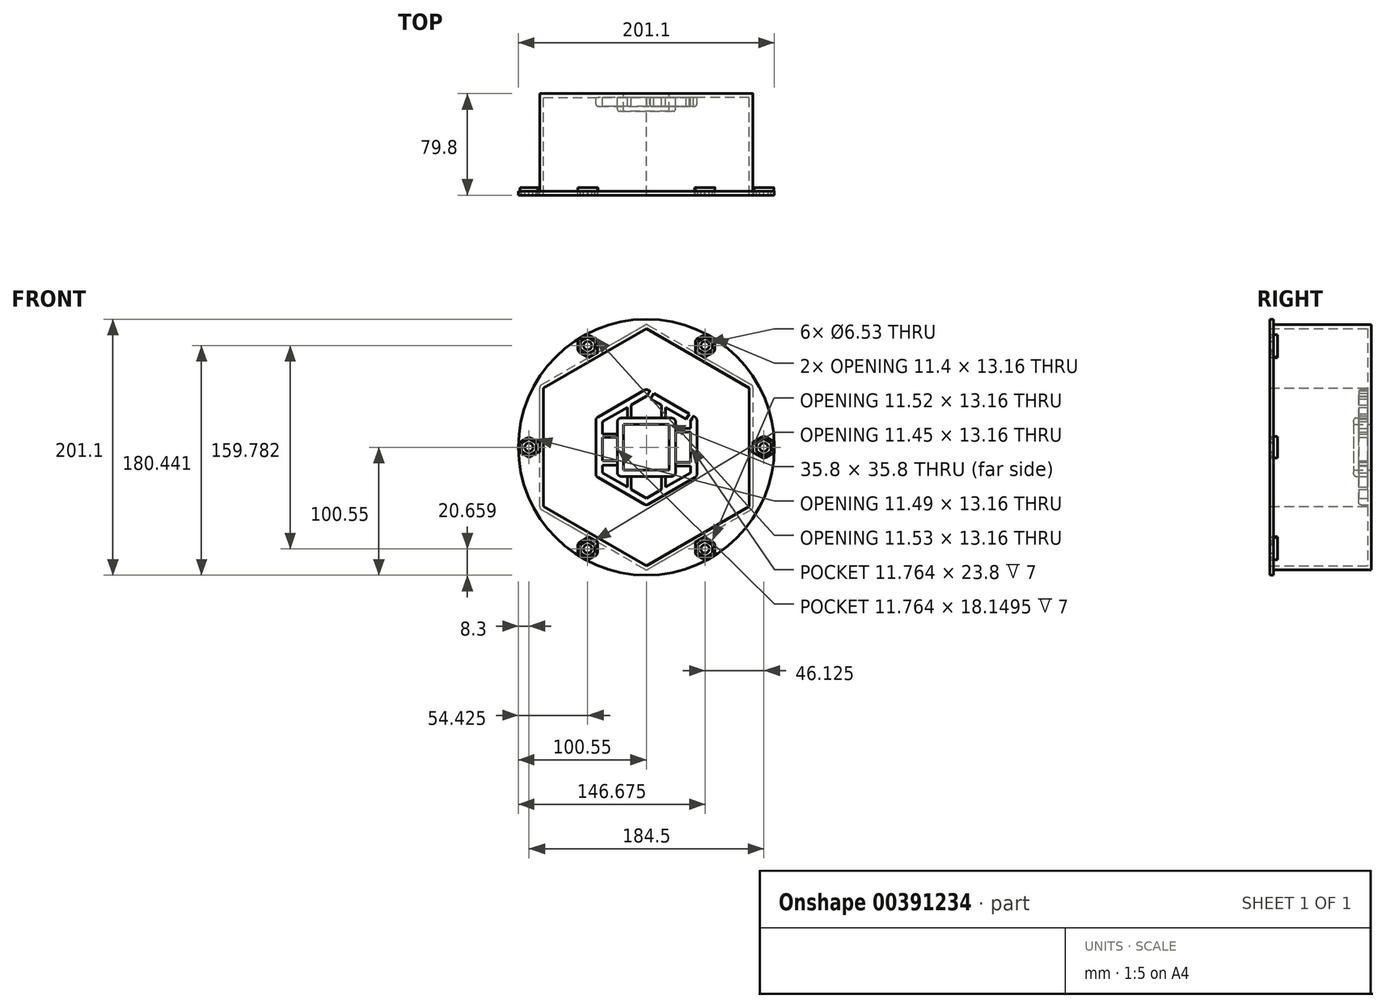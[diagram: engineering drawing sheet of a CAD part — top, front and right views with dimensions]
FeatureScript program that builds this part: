
annotation { "Feature Type Name" : "Feature", "Feature Type Description" : "" }
export const myFeature = defineFeature(function(context is Context, id is Id, definition is map)
    precondition{}
    {
        {
            var Q0;
            Q0=qCreatedBy(makeId("Front.planeOp"),FACE);
            var sketch = newSketch(context, id + "F0", { "sketchPlane" : qUnion([Q0])});
            skCircle(sketch, "E0.cCircle", {"center": v(0, 0) * mm, "radius": 80.75 * mm, "construction": true});
            skLineSegment(sketch, "E0.0", {"start": v(80.75, -46.62) * mm, "end": v(0, -93.24) * mm});
            skLineSegment(sketch, "E0.1", {"start": v(0, -93.24) * mm, "end": v(-80.75, -46.62) * mm});
            skLineSegment(sketch, "E0.2", {"start": v(-80.75, -46.62) * mm, "end": v(-80.75, 46.62) * mm});
            skLineSegment(sketch, "E0.3", {"start": v(-80.75, 46.62) * mm, "end": v(0, 93.24) * mm});
            skLineSegment(sketch, "E0.4", {"start": v(0, 93.24) * mm, "end": v(80.75, 46.62) * mm});
            skLineSegment(sketch, "E0.5", {"start": v(80.75, 46.62) * mm, "end": v(80.75, -46.62) * mm});
            skPoint(sketch, "E0.0.midPoint", {"position": v(40.38, -69.93) * mm});
            skCircle(sketch, "E1.cCircle", {"center": v(0, 0) * mm, "radius": 83.75 * mm, "construction": true});
            skLineSegment(sketch, "E1.0", {"start": v(83.75, 46.62) * mm, "end": v(83.75, -46.62) * mm});
            skLineSegment(sketch, "E1.1", {"start": v(82.25, -49.22) * mm, "end": v(1.5, -95.84) * mm});
            skLineSegment(sketch, "E1.2", {"start": v(-1.5, -95.84) * mm, "end": v(-82.25, -49.22) * mm});
            skLineSegment(sketch, "E1.3", {"start": v(-83.75, -46.62) * mm, "end": v(-83.75, 46.62) * mm});
            skLineSegment(sketch, "E1.4", {"start": v(-82.25, 49.22) * mm, "end": v(-1.5, 95.84) * mm});
            skLineSegment(sketch, "E1.5", {"start": v(1.5, 95.84) * mm, "end": v(82.25, 49.22) * mm});
            skPoint(sketch, "E1.0.midPoint", {"position": v(83.75, 0) * mm});
            skCircle(sketch, "E2", {"center": v(0, 0) * mm, "radius": 100.55 * mm});
            skCircle(sketch, "E3.cCircle", {"center": v(0, 0) * mm, "radius": 39.66 * mm, "construction": true});
            skLineSegment(sketch, "E3.0", {"start": v(38.16, -23.77) * mm, "end": v(1.5, -44.93) * mm});
            skLineSegment(sketch, "E3.1", {"start": v(-1.5, -44.93) * mm, "end": v(-38.16, -23.77) * mm});
            skLineSegment(sketch, "E3.2", {"start": v(-39.66, -21.17) * mm, "end": v(-39.66, 21.17) * mm});
            skLineSegment(sketch, "E3.3", {"start": v(-38.16, 23.77) * mm, "end": v(-1.5, 44.93) * mm});
            skLineSegment(sketch, "E3.4", {"start": v(1.5, 44.93) * mm, "end": v(38.16, 23.77) * mm});
            skLineSegment(sketch, "E3.5", {"start": v(39.66, 21.17) * mm, "end": v(39.66, -21.17) * mm});
            skPoint(sketch, "E3.0.midPoint", {"position": v(19.83, -34.35) * mm});
            skCircle(sketch, "E4.cCircle", {"center": v(0, 0) * mm, "radius": 34.66 * mm, "construction": true});
            skLineSegment(sketch, "E4.0", {"start": v(34.66, -20.01) * mm, "end": v(0, -40.03) * mm});
            skLineSegment(sketch, "E4.1", {"start": v(0, -40.03) * mm, "end": v(-34.66, -20.01) * mm});
            skLineSegment(sketch, "E4.2", {"start": v(-34.66, -20.01) * mm, "end": v(-34.66, 20.01) * mm});
            skLineSegment(sketch, "E4.3", {"start": v(-34.66, 20.01) * mm, "end": v(0, 40.03) * mm});
            skLineSegment(sketch, "E4.4", {"start": v(0, 40.03) * mm, "end": v(34.66, 20.01) * mm});
            skLineSegment(sketch, "E4.5", {"start": v(34.66, 20.01) * mm, "end": v(34.66, -20.01) * mm});
            skPoint(sketch, "E4.0.midPoint", {"position": v(17.33, -30.02) * mm});
            skPoint(sketch, "E5.visualSharp", {"position": v(0, 96.7) * mm});
            skArc(sketch, "E5.filletArc", {"start": v(1.5, 95.84) * mm, "mid": v(0, 96.24) * mm, "end": v(-1.5, 95.84) * mm});
            skPoint(sketch, "E6.visualSharp", {"position": v(83.75, 48.35) * mm});
            skArc(sketch, "E6.filletArc", {"start": v(83.75, 46.62) * mm, "mid": v(83.35, 48.12) * mm, "end": v(82.25, 49.22) * mm});
            skPoint(sketch, "E7.visualSharp", {"position": v(83.75, -48.35) * mm});
            skArc(sketch, "E7.filletArc", {"start": v(82.25, -49.22) * mm, "mid": v(83.35, -48.12) * mm, "end": v(83.75, -46.62) * mm});
            skPoint(sketch, "E8.visualSharp", {"position": v(0, -96.7) * mm});
            skArc(sketch, "E8.filletArc", {"start": v(-1.5, -95.84) * mm, "mid": v(0, -96.24) * mm, "end": v(1.5, -95.84) * mm});
            skPoint(sketch, "E9.visualSharp", {"position": v(-83.75, -48.35) * mm});
            skArc(sketch, "E9.filletArc", {"start": v(-83.75, -46.62) * mm, "mid": v(-83.35, -48.12) * mm, "end": v(-82.25, -49.22) * mm});
            skPoint(sketch, "E10.visualSharp", {"position": v(-83.75, 48.35) * mm});
            skArc(sketch, "E10.filletArc", {"start": v(-82.25, 49.22) * mm, "mid": v(-83.35, 48.12) * mm, "end": v(-83.75, 46.62) * mm});
            skPoint(sketch, "E11.visualSharp", {"position": v(39.66, 22.9) * mm});
            skArc(sketch, "E11.filletArc", {"start": v(39.66, 21.17) * mm, "mid": v(39.26, 22.67) * mm, "end": v(38.16, 23.77) * mm});
            skPoint(sketch, "E12.visualSharp", {"position": v(39.66, -22.9) * mm});
            skArc(sketch, "E12.filletArc", {"start": v(38.16, -23.77) * mm, "mid": v(39.26, -22.67) * mm, "end": v(39.66, -21.17) * mm});
            skPoint(sketch, "E13.visualSharp", {"position": v(0, -45.8) * mm});
            skArc(sketch, "E13.filletArc", {"start": v(-1.5, -44.93) * mm, "mid": v(0, -45.34) * mm, "end": v(1.5, -44.93) * mm});
            skPoint(sketch, "E14.visualSharp", {"position": v(-39.66, -22.9) * mm});
            skArc(sketch, "E14.filletArc", {"start": v(-39.66, -21.17) * mm, "mid": v(-39.26, -22.67) * mm, "end": v(-38.16, -23.77) * mm});
            skPoint(sketch, "E15.visualSharp", {"position": v(-39.66, 22.9) * mm});
            skArc(sketch, "E15.filletArc", {"start": v(-38.16, 23.77) * mm, "mid": v(-39.26, 22.67) * mm, "end": v(-39.66, 21.17) * mm});
            skPoint(sketch, "E16.visualSharp", {"position": v(0, 45.8) * mm});
            skArc(sketch, "E16.filletArc", {"start": v(1.5, 44.93) * mm, "mid": v(0, 45.34) * mm, "end": v(-1.5, 44.93) * mm});
            skPoint(sketch, "E17", {"position": v(-46.13, 79.9) * mm});
            skPoint(sketch, "E18", {"position": v(-92.25, 0) * mm});
            skPoint(sketch, "E19", {"position": v(-46.12, -79.9) * mm});
            skPoint(sketch, "E20", {"position": v(46.13, -79.9) * mm});
            skPoint(sketch, "E21", {"position": v(92.25, 0) * mm});
            skPoint(sketch, "E22", {"position": v(46.13, 79.9) * mm});
            skCircle(sketch, "E23.cCircle", {"center": v(92.25, 0) * mm, "radius": 5.7 * mm, "construction": true});
            skLineSegment(sketch, "E23.0", {"start": v(97.95, -3.3) * mm, "end": v(92.25, -6.58) * mm});
            skLineSegment(sketch, "E23.1", {"start": v(92.25, -6.58) * mm, "end": v(86.55, -3.3) * mm});
            skLineSegment(sketch, "E23.2", {"start": v(86.55, -3.3) * mm, "end": v(86.55, 3.3) * mm});
            skLineSegment(sketch, "E23.3", {"start": v(86.55, 3.3) * mm, "end": v(92.25, 6.58) * mm});
            skLineSegment(sketch, "E23.4", {"start": v(92.25, 6.58) * mm, "end": v(97.95, 3.3) * mm});
            skLineSegment(sketch, "E23.5", {"start": v(97.95, 3.3) * mm, "end": v(97.95, -3.3) * mm});
            skPoint(sketch, "E23.0.midPoint", {"position": v(95.1, -4.94) * mm});
            skCircle(sketch, "E24.cCircle", {"center": v(46.13, 79.9) * mm, "radius": 5.7 * mm, "construction": true});
            skLineSegment(sketch, "E24.0", {"start": v(51.83, 83.18) * mm, "end": v(51.83, 76.6) * mm});
            skLineSegment(sketch, "E24.1", {"start": v(51.83, 76.6) * mm, "end": v(46.13, 73.3) * mm});
            skLineSegment(sketch, "E24.2", {"start": v(46.13, 73.3) * mm, "end": v(40.43, 76.6) * mm});
            skLineSegment(sketch, "E24.3", {"start": v(40.43, 76.6) * mm, "end": v(40.43, 83.18) * mm});
            skLineSegment(sketch, "E24.4", {"start": v(40.43, 83.18) * mm, "end": v(46.12, 86.47) * mm});
            skLineSegment(sketch, "E24.5", {"start": v(46.13, 86.47) * mm, "end": v(51.83, 83.18) * mm});
            skPoint(sketch, "E24.0.midPoint", {"position": v(51.83, 79.9) * mm});
            skCircle(sketch, "E25.cCircle", {"center": v(-46.13, 79.9) * mm, "radius": 5.7 * mm, "construction": true});
            skLineSegment(sketch, "E25.0", {"start": v(-40.5, 76.48) * mm, "end": v(-46.26, 73.31) * mm});
            skLineSegment(sketch, "E25.1", {"start": v(-46.26, 73.31) * mm, "end": v(-51.9, 76.72) * mm});
            skLineSegment(sketch, "E25.2", {"start": v(-51.9, 76.72) * mm, "end": v(-51.76, 83.3) * mm});
            skLineSegment(sketch, "E25.3", {"start": v(-51.76, 83.3) * mm, "end": v(-45.99, 86.47) * mm});
            skLineSegment(sketch, "E25.4", {"start": v(-45.99, 86.47) * mm, "end": v(-40.36, 83.06) * mm});
            skLineSegment(sketch, "E25.5", {"start": v(-40.36, 83.06) * mm, "end": v(-40.5, 76.48) * mm});
            skPoint(sketch, "E25.0.midPoint", {"position": v(-43.38, 74.9) * mm});
            skCircle(sketch, "E26.cCircle", {"center": v(-92.25, 0) * mm, "radius": 5.7 * mm, "construction": true});
            skLineSegment(sketch, "E26.0", {"start": v(-86.5, -3.22) * mm, "end": v(-92.16, -6.58) * mm});
            skLineSegment(sketch, "E26.1", {"start": v(-92.16, -6.58) * mm, "end": v(-97.9, -3.37) * mm});
            skLineSegment(sketch, "E26.2", {"start": v(-97.9, -3.37) * mm, "end": v(-98, 3.22) * mm});
            skLineSegment(sketch, "E26.3", {"start": v(-98, 3.22) * mm, "end": v(-92.34, 6.58) * mm});
            skLineSegment(sketch, "E26.4", {"start": v(-92.34, 6.58) * mm, "end": v(-86.6, 3.37) * mm});
            skLineSegment(sketch, "E26.5", {"start": v(-86.6, 3.37) * mm, "end": v(-86.5, -3.22) * mm});
            skPoint(sketch, "E26.0.midPoint", {"position": v(-89.34, -4.9) * mm});
            skCircle(sketch, "E27.cCircle", {"center": v(46.13, -79.9) * mm, "radius": 5.7 * mm, "construction": true});
            skLineSegment(sketch, "E27.0", {"start": v(51.77, -83.28) * mm, "end": v(46, -86.47) * mm});
            skLineSegment(sketch, "E27.1", {"start": v(46, -86.47) * mm, "end": v(40.37, -83.08) * mm});
            skLineSegment(sketch, "E27.2", {"start": v(40.37, -83.08) * mm, "end": v(40.48, -76.5) * mm});
            skLineSegment(sketch, "E27.3", {"start": v(40.48, -76.5) * mm, "end": v(46.24, -73.31) * mm});
            skLineSegment(sketch, "E27.4", {"start": v(46.24, -73.31) * mm, "end": v(51.88, -76.7) * mm});
            skLineSegment(sketch, "E27.5", {"start": v(51.88, -76.7) * mm, "end": v(51.77, -83.28) * mm});
            skPoint(sketch, "E27.0.midPoint", {"position": v(48.89, -84.88) * mm});
            skCircle(sketch, "E28.cCircle", {"center": v(-46.12, -79.9) * mm, "radius": 5.7 * mm, "construction": true});
            skLineSegment(sketch, "E28.0", {"start": v(-40.4, -83.14) * mm, "end": v(-46.07, -86.47) * mm});
            skLineSegment(sketch, "E28.1", {"start": v(-46.07, -86.47) * mm, "end": v(-51.8, -83.23) * mm});
            skLineSegment(sketch, "E28.2", {"start": v(-51.8, -83.23) * mm, "end": v(-51.85, -76.65) * mm});
            skLineSegment(sketch, "E28.3", {"start": v(-51.85, -76.65) * mm, "end": v(-46.18, -73.3) * mm});
            skLineSegment(sketch, "E28.4", {"start": v(-46.18, -73.3) * mm, "end": v(-40.45, -76.55) * mm});
            skLineSegment(sketch, "E28.5", {"start": v(-40.45, -76.55) * mm, "end": v(-40.4, -83.14) * mm});
            skPoint(sketch, "E28.0.midPoint", {"position": v(-43.24, -84.8) * mm});
            skCircle(sketch, "E29.cCircle", {"center": v(46.13, -79.9) * mm, "radius": 7.7 * mm, "construction": true});
            skLineSegment(sketch, "E29.0", {"start": v(53.87, -77.31) * mm, "end": v(53.78, -82.74) * mm});
            skLineSegment(sketch, "E29.1", {"start": v(52.23, -85.31) * mm, "end": v(47.48, -87.94) * mm});
            skLineSegment(sketch, "E29.2", {"start": v(44.48, -87.89) * mm, "end": v(39.83, -85.1) * mm});
            skLineSegment(sketch, "E29.3", {"start": v(38.38, -82.47) * mm, "end": v(38.5, -75.3) * mm});
            skLineSegment(sketch, "E29.4", {"start": v(38.5, -75.3) * mm, "end": v(46.28, -71) * mm});
            skLineSegment(sketch, "E29.5", {"start": v(46.28, -71) * mm, "end": v(52.42, -74.7) * mm});
            skPoint(sketch, "E29.0.midPoint", {"position": v(53.82, -80.03) * mm});
            skCircle(sketch, "E30.cCircle", {"center": v(-46.12, -79.9) * mm, "radius": 7.7 * mm, "construction": true});
            skLineSegment(sketch, "E30.0", {"start": v(-39.88, -85.15) * mm, "end": v(-44.56, -87.9) * mm});
            skLineSegment(sketch, "E30.1", {"start": v(-47.56, -87.93) * mm, "end": v(-52.28, -85.25) * mm});
            skLineSegment(sketch, "E30.2", {"start": v(-53.8, -82.67) * mm, "end": v(-53.85, -77.24) * mm});
            skLineSegment(sketch, "E30.3", {"start": v(-52.37, -74.63) * mm, "end": v(-46.2, -71) * mm});
            skLineSegment(sketch, "E30.4", {"start": v(-46.2, -71) * mm, "end": v(-38.46, -75.38) * mm});
            skLineSegment(sketch, "E30.5", {"start": v(-38.46, -75.38) * mm, "end": v(-38.4, -82.54) * mm});
            skPoint(sketch, "E30.0.midPoint", {"position": v(-42.22, -86.53) * mm});
            skCircle(sketch, "E31.cCircle", {"center": v(-92.25, 0) * mm, "radius": 7.05 * mm, "construction": true});
            skLineSegment(sketch, "E31.0", {"start": v(-85.15, -3.98) * mm, "end": v(-90.66, -7.25) * mm});
            skLineSegment(sketch, "E31.1", {"start": v(-93.65, -7.3) * mm, "end": v(-97.73, -5) * mm});
            skLineSegment(sketch, "E31.2", {"start": v(-99.27, -2.43) * mm, "end": v(-99.33, 2.24) * mm});
            skLineSegment(sketch, "E31.3", {"start": v(-97.86, 4.86) * mm, "end": v(-93.84, 7.25) * mm});
            skLineSegment(sketch, "E31.4", {"start": v(-90.85, 7.3) * mm, "end": v(-85.26, 4.16) * mm});
            skLineSegment(sketch, "E31.5", {"start": v(-85.26, 4.16) * mm, "end": v(-85.15, -3.98) * mm});
            skPoint(sketch, "E31.0.midPoint", {"position": v(-88.65, -6.06) * mm});
            skCircle(sketch, "E32.cCircle", {"center": v(-46.13, 79.9) * mm, "radius": 7.7 * mm, "construction": true});
            skLineSegment(sketch, "E32.0", {"start": v(-53.83, 77.18) * mm, "end": v(-53.83, 82.6) * mm});
            skLineSegment(sketch, "E32.1", {"start": v(-52.33, 85.2) * mm, "end": v(-47.63, 87.92) * mm});
            skLineSegment(sketch, "E32.2", {"start": v(-44.63, 87.92) * mm, "end": v(-39.93, 85.2) * mm});
            skLineSegment(sketch, "E32.3", {"start": v(-38.43, 82.6) * mm, "end": v(-38.43, 75.45) * mm});
            skLineSegment(sketch, "E32.4", {"start": v(-38.43, 75.45) * mm, "end": v(-46.13, 71) * mm});
            skLineSegment(sketch, "E32.5", {"start": v(-46.13, 71) * mm, "end": v(-52.33, 74.58) * mm});
            skPoint(sketch, "E32.0.midPoint", {"position": v(-53.83, 79.9) * mm});
            skCircle(sketch, "E33.cCircle", {"center": v(46.13, 79.9) * mm, "radius": 7.7 * mm, "construction": true});
            skLineSegment(sketch, "E33.0", {"start": v(52.33, 74.58) * mm, "end": v(46.13, 71) * mm});
            skLineSegment(sketch, "E33.1", {"start": v(46.13, 71) * mm, "end": v(38.43, 75.45) * mm});
            skLineSegment(sketch, "E33.2", {"start": v(38.43, 75.45) * mm, "end": v(38.43, 82.6) * mm});
            skLineSegment(sketch, "E33.3", {"start": v(39.93, 85.2) * mm, "end": v(44.62, 87.92) * mm});
            skLineSegment(sketch, "E33.4", {"start": v(47.62, 87.92) * mm, "end": v(52.33, 85.2) * mm});
            skLineSegment(sketch, "E33.5", {"start": v(53.83, 82.6) * mm, "end": v(53.83, 77.18) * mm});
            skPoint(sketch, "E33.0.midPoint", {"position": v(49.98, 73.22) * mm});
            skCircle(sketch, "E34.cCircle", {"center": v(92.25, 0) * mm, "radius": 7.7 * mm, "construction": true});
            skLineSegment(sketch, "E34.0", {"start": v(99.95, 2.71) * mm, "end": v(99.95, -2.71) * mm});
            skLineSegment(sketch, "E34.1", {"start": v(98.45, -5.31) * mm, "end": v(93.75, -8.03) * mm});
            skLineSegment(sketch, "E34.2", {"start": v(90.75, -8.03) * mm, "end": v(84.55, -4.45) * mm});
            skLineSegment(sketch, "E34.3", {"start": v(84.55, -4.45) * mm, "end": v(84.55, 4.45) * mm});
            skLineSegment(sketch, "E34.4", {"start": v(84.55, 4.45) * mm, "end": v(90.75, 8.03) * mm});
            skLineSegment(sketch, "E34.5", {"start": v(93.75, 8.03) * mm, "end": v(98.45, 5.31) * mm});
            skPoint(sketch, "E34.0.midPoint", {"position": v(99.95, 0) * mm});
            skLineSegment(sketch, "E35", {"start": v(84.55, -4.45) * mm, "end": v(83.75, -4.45) * mm});
            skLineSegment(sketch, "E36", {"start": v(84.55, 4.45) * mm, "end": v(83.75, 4.45) * mm});
            skPoint(sketch, "E37.visualSharp", {"position": v(92.25, 8.9) * mm});
            skArc(sketch, "E37.filletArc", {"start": v(93.75, 8.03) * mm, "mid": v(92.25, 8.43) * mm, "end": v(90.75, 8.03) * mm});
            skPoint(sketch, "E38.visualSharp", {"position": v(99.95, 4.45) * mm});
            skArc(sketch, "E38.filletArc", {"start": v(99.95, 2.71) * mm, "mid": v(99.55, 4.21) * mm, "end": v(98.45, 5.31) * mm});
            skPoint(sketch, "E39.visualSharp", {"position": v(99.95, -4.45) * mm});
            skArc(sketch, "E39.filletArc", {"start": v(98.45, -5.31) * mm, "mid": v(99.55, -4.21) * mm, "end": v(99.95, -2.71) * mm});
            skPoint(sketch, "E40.visualSharp", {"position": v(92.25, -8.9) * mm});
            skArc(sketch, "E40.filletArc", {"start": v(90.75, -8.03) * mm, "mid": v(92.25, -8.43) * mm, "end": v(93.75, -8.03) * mm});
            skPoint(sketch, "E41.visualSharp", {"position": v(38.43, 84.34) * mm});
            skArc(sketch, "E41.filletArc", {"start": v(39.93, 85.2) * mm, "mid": v(38.83, 84.1) * mm, "end": v(38.43, 82.6) * mm});
            skPoint(sketch, "E42.visualSharp", {"position": v(46.12, 88.78) * mm});
            skArc(sketch, "E42.filletArc", {"start": v(47.62, 87.92) * mm, "mid": v(46.12, 88.32) * mm, "end": v(44.62, 87.92) * mm});
            skPoint(sketch, "E43.visualSharp", {"position": v(53.83, 84.34) * mm});
            skArc(sketch, "E43.filletArc", {"start": v(53.83, 82.6) * mm, "mid": v(53.42, 84.1) * mm, "end": v(52.33, 85.2) * mm});
            skPoint(sketch, "E44.visualSharp", {"position": v(53.83, 75.45) * mm});
            skArc(sketch, "E44.filletArc", {"start": v(52.33, 74.58) * mm, "mid": v(53.42, 75.68) * mm, "end": v(53.83, 77.18) * mm});
            skLineSegment(sketch, "E45", {"start": v(38.43, 75.45) * mm, "end": v(38.03, 74.75) * mm});
            skLineSegment(sketch, "E46", {"start": v(46.13, 71) * mm, "end": v(45.73, 70.3) * mm});
            skPoint(sketch, "E47.visualSharp", {"position": v(-46.13, 88.78) * mm});
            skArc(sketch, "E47.filletArc", {"start": v(-44.63, 87.92) * mm, "mid": v(-46.13, 88.32) * mm, "end": v(-47.63, 87.92) * mm});
            skPoint(sketch, "E48.visualSharp", {"position": v(-38.43, 84.34) * mm});
            skArc(sketch, "E48.filletArc", {"start": v(-38.43, 82.6) * mm, "mid": v(-38.83, 84.1) * mm, "end": v(-39.93, 85.2) * mm});
            skPoint(sketch, "E49.visualSharp", {"position": v(-53.83, 84.34) * mm});
            skArc(sketch, "E49.filletArc", {"start": v(-52.33, 85.2) * mm, "mid": v(-53.42, 84.1) * mm, "end": v(-53.83, 82.6) * mm});
            skPoint(sketch, "E50.visualSharp", {"position": v(-53.83, 75.45) * mm});
            skArc(sketch, "E50.filletArc", {"start": v(-53.83, 77.18) * mm, "mid": v(-53.42, 75.68) * mm, "end": v(-52.33, 74.58) * mm});
            skLineSegment(sketch, "E51", {"start": v(-46.13, 71) * mm, "end": v(-45.73, 70.3) * mm});
            skLineSegment(sketch, "E52", {"start": v(-38.43, 75.45) * mm, "end": v(-38.03, 74.75) * mm});
            skPoint(sketch, "E53.visualSharp", {"position": v(-92.36, 8.14) * mm});
            skArc(sketch, "E53.filletArc", {"start": v(-90.85, 7.3) * mm, "mid": v(-92.35, 7.67) * mm, "end": v(-93.84, 7.25) * mm});
            skPoint(sketch, "E54.visualSharp", {"position": v(-99.35, 3.98) * mm});
            skArc(sketch, "E54.filletArc", {"start": v(-97.86, 4.86) * mm, "mid": v(-98.94, 3.75) * mm, "end": v(-99.33, 2.24) * mm});
            skPoint(sketch, "E55.visualSharp", {"position": v(-99.24, -4.16) * mm});
            skArc(sketch, "E55.filletArc", {"start": v(-99.27, -2.43) * mm, "mid": v(-98.84, -3.92) * mm, "end": v(-97.73, -5) * mm});
            skPoint(sketch, "E56.visualSharp", {"position": v(-92.14, -8.14) * mm});
            skArc(sketch, "E56.filletArc", {"start": v(-93.65, -7.3) * mm, "mid": v(-92.15, -7.67) * mm, "end": v(-90.66, -7.25) * mm});
            skLineSegment(sketch, "E57", {"start": v(-85.26, 4.16) * mm, "end": v(-83.75, 4.18) * mm});
            skLineSegment(sketch, "E58", {"start": v(-85.15, -3.98) * mm, "end": v(-83.75, -3.96) * mm});
            skPoint(sketch, "E59.visualSharp", {"position": v(-53.86, -75.5) * mm});
            skArc(sketch, "E59.filletArc", {"start": v(-52.37, -74.63) * mm, "mid": v(-53.46, -75.74) * mm, "end": v(-53.85, -77.24) * mm});
            skPoint(sketch, "E60.visualSharp", {"position": v(-53.79, -84.4) * mm});
            skArc(sketch, "E60.filletArc", {"start": v(-53.8, -82.67) * mm, "mid": v(-53.39, -84.16) * mm, "end": v(-52.28, -85.25) * mm});
            skPoint(sketch, "E61.visualSharp", {"position": v(-46.05, -88.78) * mm});
            skArc(sketch, "E61.filletArc", {"start": v(-47.56, -87.93) * mm, "mid": v(-46.06, -88.32) * mm, "end": v(-44.56, -87.9) * mm});
            skPoint(sketch, "E62.visualSharp", {"position": v(-38.4, -84.28) * mm});
            skArc(sketch, "E62.filletArc", {"start": v(-39.88, -85.15) * mm, "mid": v(-38.8, -84.05) * mm, "end": v(-38.4, -82.54) * mm});
            skLineSegment(sketch, "E63", {"start": v(-46.2, -71) * mm, "end": v(-45.78, -70.27) * mm});
            skLineSegment(sketch, "E64", {"start": v(-38.46, -75.38) * mm, "end": v(-38.08, -74.72) * mm});
            skPoint(sketch, "E65.visualSharp", {"position": v(53.9, -75.58) * mm});
            skArc(sketch, "E65.filletArc", {"start": v(53.87, -77.31) * mm, "mid": v(53.5, -75.8) * mm, "end": v(52.42, -74.7) * mm});
            skPoint(sketch, "E66.visualSharp", {"position": v(53.74, -84.47) * mm});
            skArc(sketch, "E66.filletArc", {"start": v(52.23, -85.31) * mm, "mid": v(53.35, -84.23) * mm, "end": v(53.78, -82.74) * mm});
            skPoint(sketch, "E67.visualSharp", {"position": v(45.97, -88.78) * mm});
            skArc(sketch, "E67.filletArc", {"start": v(44.48, -87.89) * mm, "mid": v(45.97, -88.32) * mm, "end": v(47.48, -87.94) * mm});
            skPoint(sketch, "E68.visualSharp", {"position": v(38.35, -84.2) * mm});
            skArc(sketch, "E68.filletArc", {"start": v(38.38, -82.47) * mm, "mid": v(38.75, -83.97) * mm, "end": v(39.83, -85.1) * mm});
            skLineSegment(sketch, "E69", {"start": v(38.5, -75.3) * mm, "end": v(38.14, -74.68) * mm});
            skLineSegment(sketch, "E70", {"start": v(46.28, -71) * mm, "end": v(45.86, -70.23) * mm});
            skCircle(sketch, "E71.cCircle", {"center": v(0, 0) * mm, "radius": 22.9 * mm, "construction": true});
            skLineSegment(sketch, "E71.0", {"start": v(19.9, -22.9) * mm, "end": v(-19.9, -22.9) * mm});
            skLineSegment(sketch, "E71.1", {"start": v(-22.9, -19.9) * mm, "end": v(-22.9, 19.9) * mm});
            skLineSegment(sketch, "E71.2", {"start": v(-19.9, 22.9) * mm, "end": v(19.9, 22.9) * mm});
            skLineSegment(sketch, "E71.3", {"start": v(22.9, 19.9) * mm, "end": v(22.9, -19.9) * mm});
            skPoint(sketch, "E71.0.midPoint", {"position": v(0, -22.9) * mm});
            skCircle(sketch, "E72.cCircle", {"center": v(0, 0) * mm, "radius": 17.9 * mm, "construction": true});
            skLineSegment(sketch, "E72.0", {"start": v(17.9, -17.9) * mm, "end": v(-17.9, -17.9) * mm});
            skLineSegment(sketch, "E72.1", {"start": v(-17.9, -17.9) * mm, "end": v(-17.9, 17.9) * mm});
            skLineSegment(sketch, "E72.2", {"start": v(-17.9, 17.9) * mm, "end": v(17.9, 17.9) * mm});
            skLineSegment(sketch, "E72.3", {"start": v(17.9, 17.9) * mm, "end": v(17.9, -17.9) * mm});
            skPoint(sketch, "E72.0.midPoint", {"position": v(0, -17.9) * mm});
            skPoint(sketch, "E73.visualSharp", {"position": v(22.9, 22.9) * mm});
            skArc(sketch, "E73.filletArc", {"start": v(22.9, 19.9) * mm, "mid": v(22.02, 22.02) * mm, "end": v(19.9, 22.9) * mm});
            skPoint(sketch, "E74.visualSharp", {"position": v(22.9, -22.9) * mm});
            skArc(sketch, "E74.filletArc", {"start": v(19.9, -22.9) * mm, "mid": v(22.02, -22.02) * mm, "end": v(22.9, -19.9) * mm});
            skPoint(sketch, "E75.visualSharp", {"position": v(-22.9, 22.9) * mm});
            skArc(sketch, "E75.filletArc", {"start": v(-19.9, 22.9) * mm, "mid": v(-22.02, 22.02) * mm, "end": v(-22.9, 19.9) * mm});
            skPoint(sketch, "E76.visualSharp", {"position": v(-22.9, -22.9) * mm});
            skArc(sketch, "E76.filletArc", {"start": v(-22.9, -19.9) * mm, "mid": v(-22.02, -22.02) * mm, "end": v(-19.9, -22.9) * mm});
            skLineSegment(sketch, "E77", {"start": v(-14.9, 22.9) * mm, "end": v(-14.9, 31.42) * mm});
            skLineSegment(sketch, "E78", {"start": v(-11.9, 22.9) * mm, "end": v(-11.9, 33.16) * mm});
            skLineSegment(sketch, "E79", {"start": v(11.9, 22.9) * mm, "end": v(11.9, 33.16) * mm});
            skLineSegment(sketch, "E80", {"start": v(14.9, 22.9) * mm, "end": v(14.9, 31.42) * mm});
            skLineSegment(sketch, "E81", {"start": v(22.9, 14.9) * mm, "end": v(34.66, 14.9) * mm});
            skLineSegment(sketch, "E82", {"start": v(22.9, 11.9) * mm, "end": v(34.66, 11.9) * mm});
            skLineSegment(sketch, "E83", {"start": v(22.9, -14.9) * mm, "end": v(34.66, -14.9) * mm});
            skLineSegment(sketch, "E84", {"start": v(22.9, -11.9) * mm, "end": v(34.66, -11.9) * mm});
            skLineSegment(sketch, "E85", {"start": v(14.9, -22.9) * mm, "end": v(14.9, -31.42) * mm});
            skLineSegment(sketch, "E86", {"start": v(11.9, -22.9) * mm, "end": v(11.9, -33.16) * mm});
            skLineSegment(sketch, "E87", {"start": v(-14.9, -22.9) * mm, "end": v(-14.9, -31.42) * mm});
            skLineSegment(sketch, "E88", {"start": v(-11.9, -22.9) * mm, "end": v(-11.9, -33.16) * mm});
            skLineSegment(sketch, "E89", {"start": v(-22.9, 10.4) * mm, "end": v(-34.66, 10.4) * mm});
            skLineSegment(sketch, "E90", {"start": v(-22.9, 7.64) * mm, "end": v(-34.66, 7.64) * mm});
            skLineSegment(sketch, "E91", {"start": v(-22.9, -10.51) * mm, "end": v(-34.66, -10.51) * mm});
            skLineSegment(sketch, "E92", {"start": v(-22.9, -14.14) * mm, "end": v(-34.66, -14.14) * mm});
            skPoint(sketch, "E93", {"position": v(35.33, 25.4) * mm});
            skPoint(sketch, "E94", {"position": v(33.78, 26.3) * mm});
            skPoint(sketch, "E95", {"position": v(36.9, 24.5) * mm});
            skPoint(sketch, "E96", {"position": v(2.77, 44.2) * mm});
            skPoint(sketch, "E97", {"position": v(5.89, 42.4) * mm});
            skLineSegment(sketch, "E98", {"start": v(2.77, 44.2) * mm, "end": v(0.27, 39.87) * mm});
            skLineSegment(sketch, "E99", {"start": v(5.89, 42.4) * mm, "end": v(3.39, 38.07) * mm});
            skLineSegment(sketch, "E100", {"start": v(33.78, 26.3) * mm, "end": v(31.28, 21.97) * mm});
            skLineSegment(sketch, "E101", {"start": v(36.9, 24.5) * mm, "end": v(34.4, 20.17) * mm});
            skSolve(sketch);
        }
        {
            var Q0;
            Q0=makeQuery(id+"F0.imprint","IMPRINT",FACE,{"disambiguationData":[TD([[makeQuery(id+"F0.imprint","IMPRINT",EDGE,{"derivedFrom":sQuery(id+"F0.wireOp",EDGE,"E0.0")}),-1.0]])]});
            var Q1;
            Q1=makeQuery(id+"F0.imprint","IMPRINT",FACE,{"disambiguationData":[TD([[makeQuery(id+"F0.imprint","IMPRINT",EDGE,{"derivedFrom":sQuery(id+"F0.wireOp",EDGE,"E4.0")}),-1.0]])]});
            var Q2;
            Q2=makeQuery(id+"F0.imprint","IMPRINT",FACE,{"disambiguationData":[TD([[makeQuery(id+"F0.imprint","IMPRINT",EDGE,{"derivedFrom":sQuery(id+"F0.wireOp",EDGE,"E72.0")}),-1.0]])]});
            var Q3;
            {var subQ0=sQuery(id+"F0.wireOp",EDGE,"E75.filletArc");Q3=makeQuery(id+"F0.imprint","IMPRINT",FACE,{"disambiguationData":[TD([[makeQuery(id+"F0.imprint","IMPRINT",EDGE,{"derivedFrom":subQ0}),-1.0]])]});}
            var Q4;
            {var subQ0=sQuery(id+"F0.wireOp",EDGE,"E77");Q4=makeQuery(id+"F0.imprint","IMPRINT",FACE,{"disambiguationData":[TD([[makeQuery(id+"F0.imprint","IMPRINT",EDGE,{"derivedFrom":subQ0}),-1.0]])]});}
            var Q5;
            {var subQ0=sQuery(id+"F0.wireOp",EDGE,"E78");Q5=makeQuery(id+"F0.imprint","IMPRINT",FACE,{"disambiguationData":[TD([[makeQuery(id+"F0.imprint","IMPRINT",EDGE,{"derivedFrom":subQ0}),-1.0]])]});}
            var Q6;
            {var subQ0=sQuery(id+"F0.wireOp",EDGE,"E79");Q6=makeQuery(id+"F0.imprint","IMPRINT",FACE,{"disambiguationData":[TD([[makeQuery(id+"F0.imprint","IMPRINT",EDGE,{"derivedFrom":subQ0}),-1.0]])]});}
            var Q7;
            {var subQ0=sQuery(id+"F0.wireOp",EDGE,"E73.filletArc");Q7=makeQuery(id+"F0.imprint","IMPRINT",FACE,{"disambiguationData":[TD([[makeQuery(id+"F0.imprint","IMPRINT",EDGE,{"derivedFrom":subQ0}),-1.0]])]});}
            var Q8;
            {var subQ0=sQuery(id+"F0.wireOp",EDGE,"E81");Q8=makeQuery(id+"F0.imprint","IMPRINT",FACE,{"disambiguationData":[TD([[makeQuery(id+"F0.imprint","IMPRINT",EDGE,{"derivedFrom":subQ0}),-1.0]])]});}
            var Q9;
            {var subQ0=sQuery(id+"F0.wireOp",EDGE,"E82");Q9=makeQuery(id+"F0.imprint","IMPRINT",FACE,{"disambiguationData":[TD([[makeQuery(id+"F0.imprint","IMPRINT",EDGE,{"derivedFrom":subQ0}),-1.0]])]});}
            var Q10;
            {var subQ0=sQuery(id+"F0.wireOp",EDGE,"E83");Q10=makeQuery(id+"F0.imprint","IMPRINT",FACE,{"disambiguationData":[TD([[makeQuery(id+"F0.imprint","IMPRINT",EDGE,{"derivedFrom":subQ0}),1.0]])]});}
            var Q11;
            {var subQ0=sQuery(id+"F0.wireOp",EDGE,"E74.filletArc");Q11=makeQuery(id+"F0.imprint","IMPRINT",FACE,{"disambiguationData":[TD([[makeQuery(id+"F0.imprint","IMPRINT",EDGE,{"derivedFrom":subQ0}),-1.0]])]});}
            var Q12;
            {var subQ0=sQuery(id+"F0.wireOp",EDGE,"E86");Q12=makeQuery(id+"F0.imprint","IMPRINT",FACE,{"disambiguationData":[TD([[makeQuery(id+"F0.imprint","IMPRINT",EDGE,{"derivedFrom":subQ0}),-1.0]])]});}
            var Q13;
            {var subQ0=sQuery(id+"F0.wireOp",EDGE,"E87");Q13=makeQuery(id+"F0.imprint","IMPRINT",FACE,{"disambiguationData":[TD([[makeQuery(id+"F0.imprint","IMPRINT",EDGE,{"derivedFrom":subQ0}),1.0]])]});}
            var Q14;
            {var subQ0=sQuery(id+"F0.wireOp",EDGE,"E76.filletArc");Q14=makeQuery(id+"F0.imprint","IMPRINT",FACE,{"disambiguationData":[TD([[makeQuery(id+"F0.imprint","IMPRINT",EDGE,{"derivedFrom":subQ0}),-1.0]])]});}
            var Q15;
            {var subQ0=sQuery(id+"F0.wireOp",EDGE,"E91");Q15=makeQuery(id+"F0.imprint","IMPRINT",FACE,{"disambiguationData":[TD([[makeQuery(id+"F0.imprint","IMPRINT",EDGE,{"derivedFrom":subQ0}),1.0]])]});}
            var Q16;
            {var subQ0=sQuery(id+"F0.wireOp",EDGE,"E90");Q16=makeQuery(id+"F0.imprint","IMPRINT",FACE,{"disambiguationData":[TD([[makeQuery(id+"F0.imprint","IMPRINT",EDGE,{"derivedFrom":subQ0}),1.0]])]});}
            var Q17;
            {var subQ0=sQuery(id+"F0.wireOp",EDGE,"E89");Q17=makeQuery(id+"F0.imprint","IMPRINT",FACE,{"disambiguationData":[TD([[makeQuery(id+"F0.imprint","IMPRINT",EDGE,{"derivedFrom":subQ0}),1.0]])]});}
            var Q18;
            {var subQ0=sQuery(id+"F0.wireOp",EDGE,"E98");Q18=makeQuery(id+"F0.imprint","IMPRINT",FACE,{"disambiguationData":[TD([[makeQuery(id+"F0.imprint","IMPRINT",EDGE,{"derivedFrom":subQ0}),1.0]])]});}
            var Q19;
            {var subQ0=sQuery(id+"F0.wireOp",EDGE,"E100");Q19=makeQuery(id+"F0.imprint","IMPRINT",FACE,{"disambiguationData":[TD([[makeQuery(id+"F0.imprint","IMPRINT",EDGE,{"derivedFrom":subQ0}),1.0]])]});}
            extrude(context, id + "F1", {"entities" : qUnion([Q0, Q1, Q2, Q3, Q4, Q5, Q6, Q7, Q8, Q9, Q10, Q11, Q12, Q13, Q14, Q15, Q16, Q17, Q18, Q19]), "depth" : 3 * mm});
        }
        {
            var Q0;
            Q0=makeQuery(id+"F0.imprint","IMPRINT",FACE,{"disambiguationData":[TD([[makeQuery(id+"F0.imprint","IMPRINT",EDGE,{"derivedFrom":sQuery(id+"F0.wireOp",EDGE,"E3.0")}),-1.0]])]});
            extrude(context, id + "F2", {"entities" : qUnion([Q0]), "depth" : 10 * mm});
        }
        {
            var Q0;
            Q0=makeQuery(id+"F0.imprint","IMPRINT",FACE,{"disambiguationData":[TD([[makeQuery(id+"F0.imprint","IMPRINT",EDGE,{"derivedFrom":sQuery(id+"F0.wireOp",EDGE,"E0.0")}),1.0]])]});
            extrude(context, id + "F3", {"entities" : qUnion([Q0]), "operationType" : NewBodyOperationType.ADD, "depth" : 79.8 * mm});
        }
        {
            var Q0;
            Q0=makeQuery(id+"F0.imprint","IMPRINT",FACE,{"disambiguationData":[TD([[makeQuery(id+"F0.imprint","IMPRINT",EDGE,{"derivedFrom":sQuery(id+"F0.wireOp",EDGE,"E1.0")}),1.0]])]});
            var Q1;
            Q1=makeQuery(id+"F0.imprint","IMPRINT",FACE,{"disambiguationData":[TD([[makeQuery(id+"F0.imprint","IMPRINT",EDGE,{"derivedFrom":sQuery(id+"F0.wireOp",EDGE,"E25.0")}),-1.0]])]});
            var Q2;
            Q2=makeQuery(id+"F0.imprint","IMPRINT",FACE,{"disambiguationData":[TD([[makeQuery(id+"F0.imprint","IMPRINT",EDGE,{"derivedFrom":sQuery(id+"F0.wireOp",EDGE,"E24.0")}),-1.0]])]});
            var Q3;
            Q3=makeQuery(id+"F0.imprint","IMPRINT",FACE,{"disambiguationData":[TD([[makeQuery(id+"F0.imprint","IMPRINT",EDGE,{"derivedFrom":sQuery(id+"F0.wireOp",EDGE,"E23.0")}),-1.0]])]});
            var Q4;
            Q4=makeQuery(id+"F0.imprint","IMPRINT",FACE,{"disambiguationData":[TD([[makeQuery(id+"F0.imprint","IMPRINT",EDGE,{"derivedFrom":sQuery(id+"F0.wireOp",EDGE,"E27.0")}),-1.0]])]});
            var Q5;
            Q5=makeQuery(id+"F0.imprint","IMPRINT",FACE,{"disambiguationData":[TD([[makeQuery(id+"F0.imprint","IMPRINT",EDGE,{"derivedFrom":sQuery(id+"F0.wireOp",EDGE,"E28.0")}),-1.0]])]});
            var Q6;
            Q6=makeQuery(id+"F0.imprint","IMPRINT",FACE,{"disambiguationData":[TD([[makeQuery(id+"F0.imprint","IMPRINT",EDGE,{"derivedFrom":sQuery(id+"F0.wireOp",EDGE,"E26.0")}),-1.0]])]});
            extrude(context, id + "F4", {"entities" : qUnion([Q0, Q1, Q2, Q3, Q4, Q5, Q6]), "operationType" : NewBodyOperationType.ADD, "depth" : 79.8 * mm, "hasSecondDirection" : true, "secondDirectionOppositeDirection" : false, "secondDirectionDepth" : 76.8 * mm});
        }
        {
            var Q0;
            Q0=makeQuery(id+"F2.opExtrude","CAP_EDGE",EDGE,{"disambiguationData":[OSD([sQuery(id+"F0.wireOp",EDGE,"E3.4")])],"isStart":false});
            fillet(context, id + "F5", {"entities" : qUnion([Q0]), "radius" : 2 * mm, "tangentPropagation" : true, "allowEdgeOverflow" : false});
        }
        {
            var Q0;
            Q0=makeQuery(id+"F0.imprint","IMPRINT",FACE,{"disambiguationData":[TD([[makeQuery(id+"F0.imprint","IMPRINT",EDGE,{"derivedFrom":sQuery(id+"F0.wireOp",EDGE,"E25.0")}),1.0]])]});
            var Q1;
            Q1=makeQuery(id+"F0.imprint","IMPRINT",FACE,{"disambiguationData":[TD([[makeQuery(id+"F0.imprint","IMPRINT",EDGE,{"derivedFrom":sQuery(id+"F0.wireOp",EDGE,"E32.4")}),1.0]])]});
            var Q2;
            Q2=makeQuery(id+"F0.imprint","IMPRINT",FACE,{"disambiguationData":[TD([[makeQuery(id+"F0.imprint","IMPRINT",EDGE,{"derivedFrom":sQuery(id+"F0.wireOp",EDGE,"E24.0")}),1.0]])]});
            var Q3;
            Q3=makeQuery(id+"F0.imprint","IMPRINT",FACE,{"disambiguationData":[TD([[makeQuery(id+"F0.imprint","IMPRINT",EDGE,{"derivedFrom":sQuery(id+"F0.wireOp",EDGE,"E33.1")}),1.0]])]});
            var Q4;
            Q4=makeQuery(id+"F0.imprint","IMPRINT",FACE,{"disambiguationData":[TD([[makeQuery(id+"F0.imprint","IMPRINT",EDGE,{"derivedFrom":sQuery(id+"F0.wireOp",EDGE,"E23.0")}),1.0]])]});
            var Q5;
            Q5=makeQuery(id+"F0.imprint","IMPRINT",FACE,{"disambiguationData":[TD([[makeQuery(id+"F0.imprint","IMPRINT",EDGE,{"derivedFrom":sQuery(id+"F0.wireOp",EDGE,"E34.3")}),1.0]])]});
            var Q6;
            Q6=makeQuery(id+"F0.imprint","IMPRINT",FACE,{"disambiguationData":[TD([[makeQuery(id+"F0.imprint","IMPRINT",EDGE,{"derivedFrom":sQuery(id+"F0.wireOp",EDGE,"E27.0")}),1.0]])]});
            var Q7;
            Q7=makeQuery(id+"F0.imprint","IMPRINT",FACE,{"disambiguationData":[TD([[makeQuery(id+"F0.imprint","IMPRINT",EDGE,{"derivedFrom":sQuery(id+"F0.wireOp",EDGE,"E29.4")}),1.0]])]});
            var Q8;
            Q8=makeQuery(id+"F0.imprint","IMPRINT",FACE,{"disambiguationData":[TD([[makeQuery(id+"F0.imprint","IMPRINT",EDGE,{"derivedFrom":sQuery(id+"F0.wireOp",EDGE,"E28.0")}),1.0]])]});
            var Q9;
            Q9=makeQuery(id+"F0.imprint","IMPRINT",FACE,{"disambiguationData":[TD([[makeQuery(id+"F0.imprint","IMPRINT",EDGE,{"derivedFrom":sQuery(id+"F0.wireOp",EDGE,"E30.4")}),1.0]])]});
            var Q10;
            Q10=makeQuery(id+"F0.imprint","IMPRINT",FACE,{"disambiguationData":[TD([[makeQuery(id+"F0.imprint","IMPRINT",EDGE,{"derivedFrom":sQuery(id+"F0.wireOp",EDGE,"E26.0")}),1.0]])]});
            var Q11;
            Q11=makeQuery(id+"F0.imprint","IMPRINT",FACE,{"disambiguationData":[TD([[makeQuery(id+"F0.imprint","IMPRINT",EDGE,{"derivedFrom":sQuery(id+"F0.wireOp",EDGE,"E31.5")}),1.0]])]});
            extrude(context, id + "F6", {"entities" : qUnion([Q0, Q1, Q2, Q3, Q4, Q5, Q6, Q7, Q8, Q9, Q10, Q11]), "depth" : 79.8 * mm, "hasSecondDirection" : true, "secondDirectionOppositeDirection" : false, "secondDirectionDepth" : 73.8 * mm});
        }
        {
            var Q0;
            Q0=sQuery(id+"F0.wireOp",VERTEX,"E17");
            var Q1;
            Q1=sQuery(id+"F0.wireOp",VERTEX,"E22");
            var Q2;
            Q2=sQuery(id+"F0.wireOp",VERTEX,"E21");
            var Q3;
            Q3=sQuery(id+"F0.wireOp",VERTEX,"E20");
            var Q4;
            Q4=sQuery(id+"F0.wireOp",VERTEX,"E19");
            var Q5;
            Q5=sQuery(id+"F0.wireOp",VERTEX,"E18");
            var Q6;
            Q6=makeQuery(id+"F4.opExtrude","SWEPT_BODY",BODY,{"disambiguationData":[OSD([sQuery(id+"F0.wireOp",EDGE,"E23.0"),sQuery(id+"F0.wireOp",EDGE,"E23.1"),sQuery(id+"F0.wireOp",EDGE,"E23.2"),sQuery(id+"F0.wireOp",EDGE,"E23.3"),sQuery(id+"F0.wireOp",EDGE,"E23.4"),sQuery(id+"F0.wireOp",EDGE,"E23.5")])]});
            var Q7;
            Q7=makeQuery(id+"F4.opExtrude","SWEPT_BODY",BODY,{"disambiguationData":[OSD([sQuery(id+"F0.wireOp",EDGE,"E24.0"),sQuery(id+"F0.wireOp",EDGE,"E24.1"),sQuery(id+"F0.wireOp",EDGE,"E24.2"),sQuery(id+"F0.wireOp",EDGE,"E24.3"),sQuery(id+"F0.wireOp",EDGE,"E24.4"),sQuery(id+"F0.wireOp",EDGE,"E24.5")])]});
            var Q8;
            Q8=makeQuery(id+"F4.opExtrude","SWEPT_BODY",BODY,{"disambiguationData":[OSD([sQuery(id+"F0.wireOp",EDGE,"E25.0"),sQuery(id+"F0.wireOp",EDGE,"E25.1"),sQuery(id+"F0.wireOp",EDGE,"E25.2"),sQuery(id+"F0.wireOp",EDGE,"E25.3"),sQuery(id+"F0.wireOp",EDGE,"E25.4"),sQuery(id+"F0.wireOp",EDGE,"E25.5")])]});
            var Q9;
            Q9=makeQuery(id+"F4.opExtrude","SWEPT_BODY",BODY,{"disambiguationData":[OSD([sQuery(id+"F0.wireOp",EDGE,"E26.0"),sQuery(id+"F0.wireOp",EDGE,"E26.1"),sQuery(id+"F0.wireOp",EDGE,"E26.2"),sQuery(id+"F0.wireOp",EDGE,"E26.3"),sQuery(id+"F0.wireOp",EDGE,"E26.4"),sQuery(id+"F0.wireOp",EDGE,"E26.5")])]});
            var Q10;
            Q10=makeQuery(id+"F4.opExtrude","SWEPT_BODY",BODY,{"disambiguationData":[OSD([sQuery(id+"F0.wireOp",EDGE,"E27.0"),sQuery(id+"F0.wireOp",EDGE,"E27.1"),sQuery(id+"F0.wireOp",EDGE,"E27.2"),sQuery(id+"F0.wireOp",EDGE,"E27.3"),sQuery(id+"F0.wireOp",EDGE,"E27.4"),sQuery(id+"F0.wireOp",EDGE,"E27.5")])]});
            var Q11;
            Q11=makeQuery(id+"F4.opExtrude","SWEPT_BODY",BODY,{"disambiguationData":[OSD([sQuery(id+"F0.wireOp",EDGE,"E28.0"),sQuery(id+"F0.wireOp",EDGE,"E28.1"),sQuery(id+"F0.wireOp",EDGE,"E28.2"),sQuery(id+"F0.wireOp",EDGE,"E28.3"),sQuery(id+"F0.wireOp",EDGE,"E28.4"),sQuery(id+"F0.wireOp",EDGE,"E28.5")])]});
            hole(context, id + "F7", {"style" : HoleStyle.SIMPLE, "endStyle" : HoleEndStyle.THROUGH, "oppositeDirection" : true, "standardTappedOrClearance" : lookupTablePath({ "standard" : "ANSI", "fit" : "Close", "size" : "1/4", "type" : "Clearance" }), "standardBlindInLast" : lookupTablePath({ "fit" : "Close", "standard" : "ANSI", "size" : "1/4", "type" : "Clearance" }), "holeDiameter" : 6.53 * mm, "tappedDepth" : 12 * mm, "tapClearance" : 3, "locations" : qUnion([Q0, Q1, Q2, Q3, Q4, Q5]), "scope" : qUnion([Q6, Q7, Q8, Q9, Q10, Q11])});
        }
        {
            var Q0;
            Q0=makeQuery(id+"F0.imprint","IMPRINT",FACE,{"disambiguationData":[TD([[makeQuery(id+"F0.imprint","IMPRINT",EDGE,{"derivedFrom":sQuery(id+"F0.wireOp",EDGE,"E71.0")}),-1.0]])]});
            extrude(context, id + "F8", {"entities" : qUnion([Q0]), "depth" : 14 * mm});
        }
        {
            var Q0;
            Q0=makeQuery(id+"F8.opExtrude","CAP_EDGE",EDGE,{"disambiguationData":[OSD([sQuery(id+"F0.wireOp",EDGE,"E71.3")])],"isStart":false});
            var Q1;
            {var subQ0=sQuery(id+"F0.wireOp",EDGE,"E71.3");var subQ1=sQuery(id+"F0.wireOp",EDGE,"E71.2");Q1=makeQuery(id+"FUb84Lql3Qi620s_4.opFillet","BLEND_EDGE",EDGE,{"blendedFrom":[makeQuery(id+"F8.opExtrude","SWEPT_EDGE",EDGE,{"disambiguationData":[OSD([subQ1,subQ0])]}),makeQuery(id+"F8.opExtrude","CAP_FACE",FACE,{"disambiguationData":[OSD([sQuery(id+"F0.wireOp",EDGE,"E71.0"),sQuery(id+"F0.wireOp",EDGE,"E71.1"),subQ1,subQ0,sQuery(id+"F0.wireOp",EDGE,"E72.0"),sQuery(id+"F0.wireOp",EDGE,"E72.1"),sQuery(id+"F0.wireOp",EDGE,"E72.2"),sQuery(id+"F0.wireOp",EDGE,"E72.3")])],"isStart":false})],"blendedInto":[makeQuery(id+"F8.opExtrude","CAP_FACE",FACE,{"disambiguationData":[OSD([sQuery(id+"F0.wireOp",EDGE,"E71.0"),sQuery(id+"F0.wireOp",EDGE,"E71.1"),subQ1,subQ0,sQuery(id+"F0.wireOp",EDGE,"E72.0"),sQuery(id+"F0.wireOp",EDGE,"E72.1"),sQuery(id+"F0.wireOp",EDGE,"E72.2"),sQuery(id+"F0.wireOp",EDGE,"E72.3")])],"isStart":false})]});}
            fillet(context, id + "F9", {"entities" : qUnion([Q0, Q1]), "radius" : 2 * mm, "tangentPropagation" : true, "allowEdgeOverflow" : false});
        }
        {
            var Q0;
            {var subQ0=sQuery(id+"F0.wireOp",EDGE,"E91");Q0=makeQuery(id+"F0.imprint","IMPRINT",FACE,{"disambiguationData":[TD([[makeQuery(id+"F0.imprint","IMPRINT",EDGE,{"derivedFrom":subQ0}),1.0]])]});}
            var Q1;
            {var subQ0=sQuery(id+"F0.wireOp",EDGE,"E89");Q1=makeQuery(id+"F0.imprint","IMPRINT",FACE,{"disambiguationData":[TD([[makeQuery(id+"F0.imprint","IMPRINT",EDGE,{"derivedFrom":subQ0}),1.0]])]});}
            var Q2;
            {var subQ0=sQuery(id+"F0.wireOp",EDGE,"E77");Q2=makeQuery(id+"F0.imprint","IMPRINT",FACE,{"disambiguationData":[TD([[makeQuery(id+"F0.imprint","IMPRINT",EDGE,{"derivedFrom":subQ0}),-1.0]])]});}
            var Q3;
            {var subQ0=sQuery(id+"F0.wireOp",EDGE,"E79");Q3=makeQuery(id+"F0.imprint","IMPRINT",FACE,{"disambiguationData":[TD([[makeQuery(id+"F0.imprint","IMPRINT",EDGE,{"derivedFrom":subQ0}),-1.0]])]});}
            var Q4;
            {var subQ0=sQuery(id+"F0.wireOp",EDGE,"E81");Q4=makeQuery(id+"F0.imprint","IMPRINT",FACE,{"disambiguationData":[TD([[makeQuery(id+"F0.imprint","IMPRINT",EDGE,{"derivedFrom":subQ0}),-1.0]])]});}
            var Q5;
            {var subQ0=sQuery(id+"F0.wireOp",EDGE,"E83");Q5=makeQuery(id+"F0.imprint","IMPRINT",FACE,{"disambiguationData":[TD([[makeQuery(id+"F0.imprint","IMPRINT",EDGE,{"derivedFrom":subQ0}),1.0]])]});}
            var Q6;
            {var subQ0=sQuery(id+"F0.wireOp",EDGE,"E85");Q6=makeQuery(id+"F0.imprint","IMPRINT",FACE,{"disambiguationData":[TD([[makeQuery(id+"F0.imprint","IMPRINT",EDGE,{"derivedFrom":subQ0}),-1.0]])]});}
            var Q7;
            {var subQ0=sQuery(id+"F0.wireOp",EDGE,"E87");Q7=makeQuery(id+"F0.imprint","IMPRINT",FACE,{"disambiguationData":[TD([[makeQuery(id+"F0.imprint","IMPRINT",EDGE,{"derivedFrom":subQ0}),1.0]])]});}
            var Q8;
            {var subQ3=sQuery(id+"F0.wireOp",EDGE,"E99");Q8=makeQuery(id+"F0.imprint","IMPRINT",FACE,{"disambiguationData":[TD([[makeQuery(id+"F0.imprint","IMPRINT",EDGE,{"derivedFrom":subQ3}),1.0]])]});}
            extrude(context, id + "F10", {"entities" : qUnion([Q0, Q1, Q2, Q3, Q4, Q5, Q6, Q7, Q8]), "operationType" : NewBodyOperationType.ADD, "depth" : 10 * mm});
        }
    });
